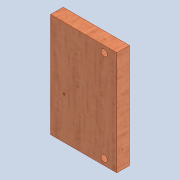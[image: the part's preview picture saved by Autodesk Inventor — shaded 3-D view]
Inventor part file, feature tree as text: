
AUTODESK INVENTOR PART (.ipt)
format: ipt  version: 2020 (Build 240168000, 168)  size: 112,640 bytes
history: native  units: mm
features: sketch x2, extrude x1, hole x1
ambient origin geometry x8: Origin, YZ Plane, XZ Plane, XY Plane, X Axis, Y Axis, Z Axis, Center Point
bodies: Solid1 (feature_tree)
feature tree (4):
  extrude  "Extrusion1"  Depth=66.0mm
  hole  "Hole1"  [1 undecoded]
  sketch  "Sketch1"  dims[d0=42.0mm d1=66.0mm]
  sketch  "Sketch4"  dims[d2=8.0mm d3=0.0mm d19=4.0mm d20=4.0mm d21=8.0mm d22=4.0mm d23=6.0mm d24=4.0mm d25=2.0mm d26=90.0deg d27=8.0mm d28=20.594885mm]
note: 1 required parameter value undecoded (feature->parameter linkage not recoverable at this tier; creation-order binding heuristic only, values carry confidence <= 0.55)
